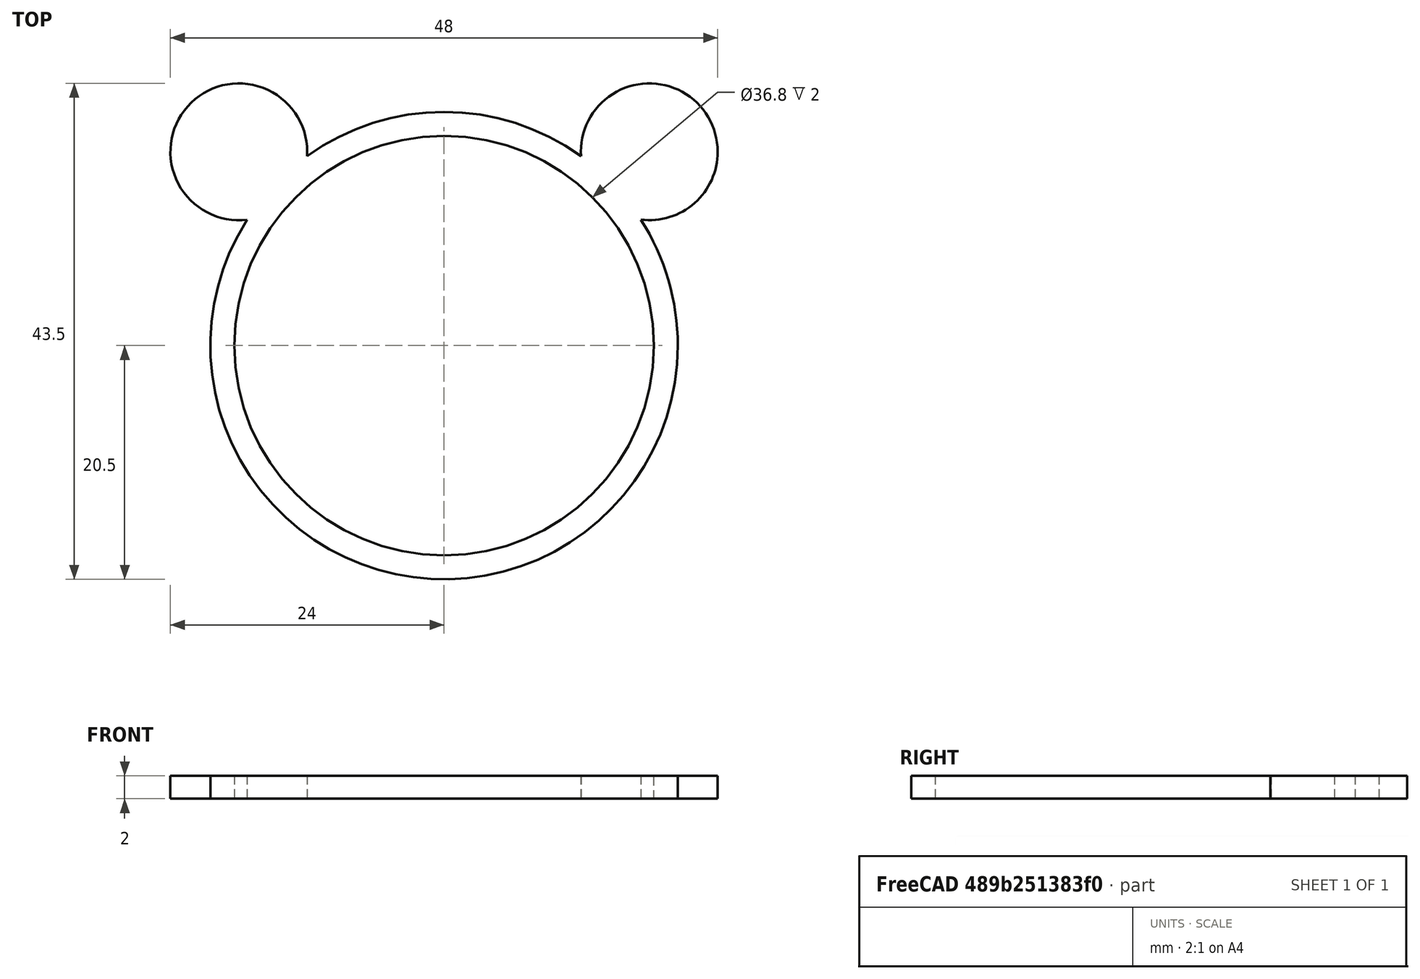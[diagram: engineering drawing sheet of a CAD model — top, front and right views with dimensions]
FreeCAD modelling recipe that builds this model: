
FCSTD DOCUMENT  (FreeCAD 0.20R29177 +233 (Git))
Label: reto_6
License: Creative Commons Attribution-ShareAlike
LicenseURL: http://creativecommons.org/licenses/by-sa/4.0/
objects: Part::Cylinder×4, Part::Cut×1, Part::MultiFuse×1
note: 6 computed .brp shape members not serialized (recipe doc carries the construction recipe); baked Part::Feature solids carry a one-line shape summary decoded from their .brp

FEATURE [Part::Cylinder] Cylinder
  Angle = 360
  AttacherType = Attacher::AttachEngine3D
  FirstAngle = 0
  Height = 2
  Radius = 20.5
  SecondAngle = 0
FEATURE [Part::Cylinder] Cylinder001
  Angle = 360
  AttacherType = Attacher::AttachEngine3D
  FirstAngle = 0
  Height = 10
  Placement = pos=(0,0,-3) rot=(0,0,1;0rad)
  Radius = 18.4
  SecondAngle = 0
FEATURE [Part::Cut] Cut  label="cuerpo_anillo"
  Base = -> Cylinder
  Refine = true
  Tool = -> Cylinder001
FEATURE [Part::Cylinder] Cylinder002
  Angle = 360
  AttacherType = Attacher::AttachEngine3D
  FirstAngle = 0
  Height = 2
  Placement = pos=(-18,17,0) rot=(0,0,1;0rad)
  Radius = 6
  SecondAngle = 0
FEATURE [Part::Cylinder] Cylinder003
  Angle = 360
  AttacherType = Attacher::AttachEngine3D
  FirstAngle = 0
  Height = 2
  Placement = pos=(12,17,0) rot=(0,0,1;0rad)
  Radius = 6
  SecondAngle = 0
FEATURE [Part::MultiFuse] Fusion
  Refine = true
  Shapes = -> [Cylinder002,Cut,Cylinder003]
